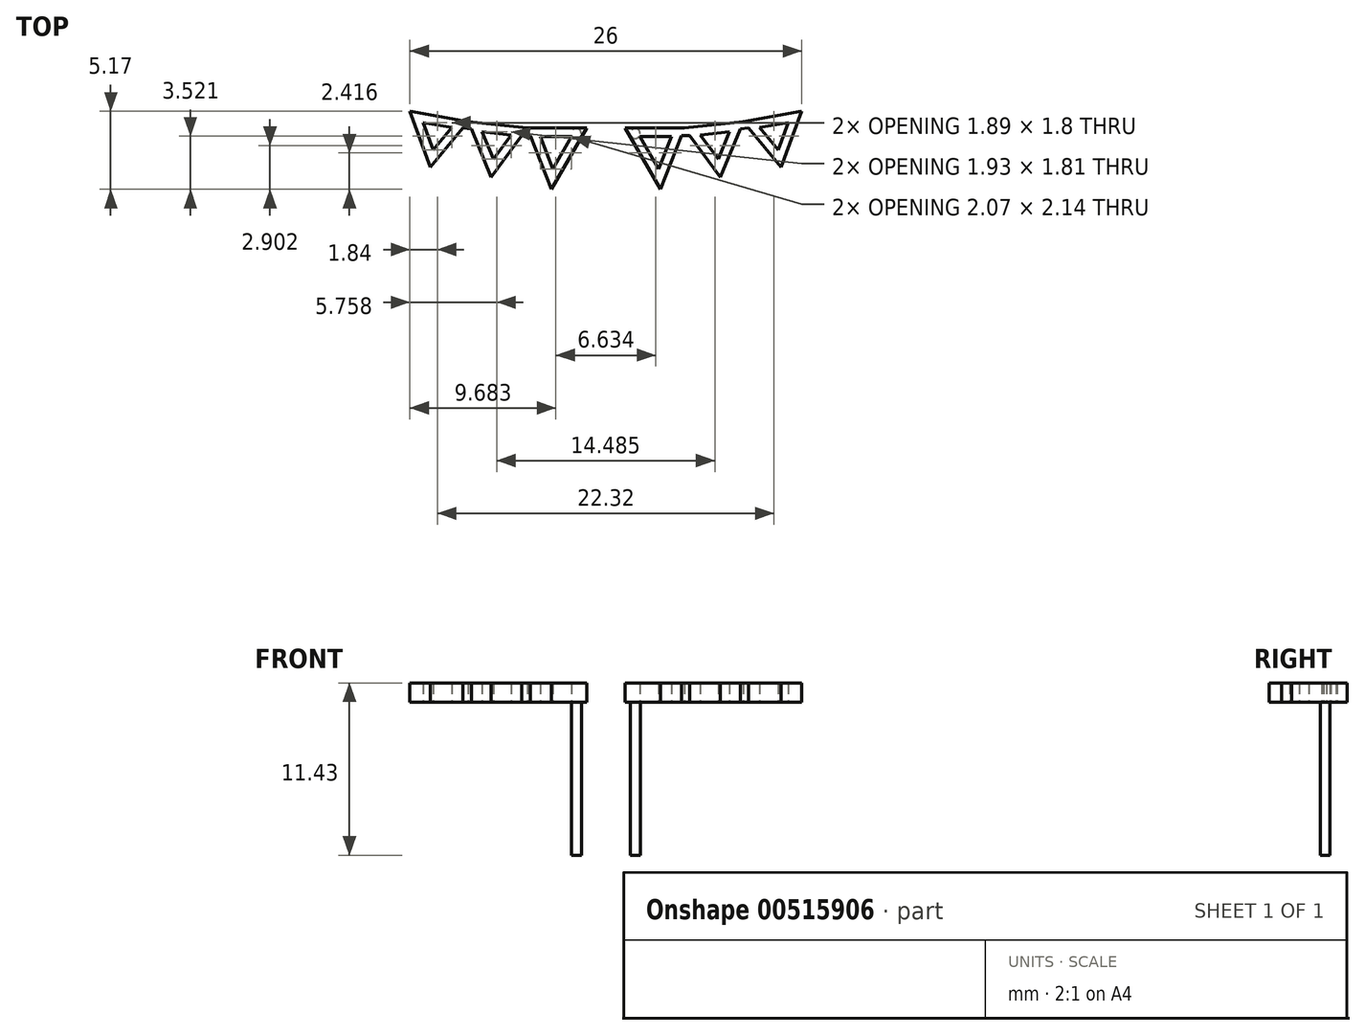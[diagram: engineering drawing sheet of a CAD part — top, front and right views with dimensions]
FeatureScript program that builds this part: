
annotation { "Feature Type Name" : "Feature", "Feature Type Description" : "" }
export const myFeature = defineFeature(function(context is Context, id is Id, definition is map)
    precondition{}
    {
        {
            var Q0;
            Q0=qCreatedBy(makeId("Top.planeOp"),FACE);
            var sketch = newSketch(context, id + "F0", { "sketchPlane" : qUnion([Q0])});
            skLineSegment(sketch, "E0", {"start": v(0, 0) * mm, "end": v(3.94, 0) * mm});
            skLineSegment(sketch, "E1", {"start": v(3.94, 0) * mm, "end": v(7.85, 0.43) * mm});
            skLineSegment(sketch, "E2", {"start": v(7.85, 0.43) * mm, "end": v(11.73, 1.1) * mm});
            skLineSegment(sketch, "E3", {"start": v(11.73, 1.1) * mm, "end": v(10.37, -2.6) * mm});
            skLineSegment(sketch, "E4", {"start": v(10.37, -2.6) * mm, "end": v(8.2, 0) * mm});
            skLineSegment(sketch, "E5", {"start": v(7.65, -0.06) * mm, "end": v(6.33, -3.26) * mm});
            skLineSegment(sketch, "E6", {"start": v(6.33, -3.26) * mm, "end": v(4.3, -0.5) * mm});
            skLineSegment(sketch, "E7", {"start": v(0, 0) * mm, "end": v(2.35, -4.07) * mm});
            skLineSegment(sketch, "E8", {"start": v(2.35, -4.07) * mm, "end": v(3.74, -0.5) * mm});
            skLineSegment(sketch, "E9.0", {"start": v(1.01, -0.58) * mm, "end": v(3.08, -0.58) * mm});
            skLineSegment(sketch, "E9.1", {"start": v(1.01, -0.58) * mm, "end": v(2.25, -2.72) * mm});
            skLineSegment(sketch, "E9.2", {"start": v(2.25, -2.72) * mm, "end": v(3.08, -0.58) * mm});
            skLineSegment(sketch, "E10.0", {"start": v(5, -0.47) * mm, "end": v(6.94, -0.26) * mm});
            skLineSegment(sketch, "E10.1", {"start": v(6.19, -2.08) * mm, "end": v(5, -0.47) * mm});
            skLineSegment(sketch, "E10.2", {"start": v(6.94, -0.26) * mm, "end": v(6.19, -2.08) * mm});
            skLineSegment(sketch, "E11.0", {"start": v(8.95, 0.02) * mm, "end": v(10.83, 0.35) * mm});
            skLineSegment(sketch, "E11.1", {"start": v(10.17, -1.45) * mm, "end": v(8.95, 0.02) * mm});
            skLineSegment(sketch, "E11.2", {"start": v(10.83, 0.35) * mm, "end": v(10.17, -1.45) * mm});
            skLineSegment(sketch, "E12", {"start": v(3.74, -0.5) * mm, "end": v(4.3, -0.5) * mm});
            skLineSegment(sketch, "E13", {"start": v(7.65, -0.06) * mm, "end": v(8.2, 0) * mm});
            skSolve(sketch);
        }
        {
            var Q0;
            Q0=makeQuery(id+"F0.imprint","IMPRINT",FACE,{"disambiguationData":[TD([[makeQuery(id+"F0.imprint","IMPRINT",EDGE,{"derivedFrom":sQuery(id+"F0.wireOp",EDGE,"E0")}),-1.0]])]});
            var Q1;
            Q1=makeQuery(id+"F0.imprint","IMPRINT",FACE,{"disambiguationData":[TD([[makeQuery(id+"F0.imprint","IMPRINT",EDGE,{"derivedFrom":sQuery(id+"F0.wireOp",EDGE,"E1")}),-1.0]])]});
            var Q2;
            Q2=makeQuery(id+"F0.imprint","IMPRINT",FACE,{"disambiguationData":[TD([[makeQuery(id+"F0.imprint","IMPRINT",EDGE,{"derivedFrom":sQuery(id+"F0.wireOp",EDGE,"E2")}),-1.0]])]});
            extrude(context, id + "F1", {"entities" : qUnion([Q0, Q1, Q2]), "depth" : 1.27 * mm, "offsetDistance" : 25.4 * mm});
        }
        {
            var Q0;
            Q0=makeQuery(id+"F1.opExtrude","CAP_FACE",FACE,{"disambiguationData":[OSD([sQuery(id+"F0.wireOp",EDGE,"E0"),sQuery(id+"F0.wireOp",EDGE,"E1"),sQuery(id+"F0.wireOp",EDGE,"E2"),sQuery(id+"F0.wireOp",EDGE,"E3"),sQuery(id+"F0.wireOp",EDGE,"E4"),sQuery(id+"F0.wireOp",EDGE,"E5"),sQuery(id+"F0.wireOp",EDGE,"E6"),sQuery(id+"F0.wireOp",EDGE,"E7"),sQuery(id+"F0.wireOp",EDGE,"E8"),sQuery(id+"F0.wireOp",EDGE,"E9.0"),sQuery(id+"F0.wireOp",EDGE,"E9.1"),sQuery(id+"F0.wireOp",EDGE,"E9.2"),sQuery(id+"F0.wireOp",EDGE,"E10.0"),sQuery(id+"F0.wireOp",EDGE,"E10.1"),sQuery(id+"F0.wireOp",EDGE,"E10.2"),sQuery(id+"F0.wireOp",EDGE,"E11.0"),sQuery(id+"F0.wireOp",EDGE,"E11.1"),sQuery(id+"F0.wireOp",EDGE,"E11.2"),sQuery(id+"F0.wireOp",EDGE,"E12"),sQuery(id+"F0.wireOp",EDGE,"E13")])],"isStart":true});
            var sketch = newSketch(context, id + "F2", { "sketchPlane" : qUnion([Q0])});
            skCircle(sketch, "E14", {"center": v(0.68, 0.37) * mm, "radius": 0.33 * mm});
            skSolve(sketch);
        }
        {
            var Q0;
            Q0 = qSketchRegion(id + "F2", true);
            extrude(context, id + "F3", {"entities" : qUnion([Q0]), "operationType" : NewBodyOperationType.ADD, "depth" : 10.16 * mm, "offsetDistance" : 25.4 * mm});
        }
        {
            var Q0;
            Q0=qCreatedBy(makeId("Right.planeOp"),FACE);
            cPlane(context, id + "F4", {"entities" : qUnion([Q0]), "cplaneType" : CPlaneType.OFFSET, "offset" : 1.27 * mm, "oppositeDirection" : true, "width" : 152.4 * mm, "height" : 152.4 * mm});
        }
        {
            var Q0;
            Q0=makeQuery(id+"F1.opExtrude","SWEPT_BODY",BODY,{"disambiguationData":[OSD([sQuery(id+"F0.wireOp",EDGE,"E0"),sQuery(id+"F0.wireOp",EDGE,"E1"),sQuery(id+"F0.wireOp",EDGE,"E2"),sQuery(id+"F0.wireOp",EDGE,"E3"),sQuery(id+"F0.wireOp",EDGE,"E4"),sQuery(id+"F0.wireOp",EDGE,"E5"),sQuery(id+"F0.wireOp",EDGE,"E6"),sQuery(id+"F0.wireOp",EDGE,"E7"),sQuery(id+"F0.wireOp",EDGE,"E8"),sQuery(id+"F0.wireOp",EDGE,"E9.0"),sQuery(id+"F0.wireOp",EDGE,"E9.1"),sQuery(id+"F0.wireOp",EDGE,"E9.2"),sQuery(id+"F0.wireOp",EDGE,"E10.0"),sQuery(id+"F0.wireOp",EDGE,"E10.1"),sQuery(id+"F0.wireOp",EDGE,"E10.2"),sQuery(id+"F0.wireOp",EDGE,"E11.0"),sQuery(id+"F0.wireOp",EDGE,"E11.1"),sQuery(id+"F0.wireOp",EDGE,"E11.2"),sQuery(id+"F0.wireOp",EDGE,"E12"),sQuery(id+"F0.wireOp",EDGE,"E13")])]});
            var Q1;
            Q1=qCreatedBy(id+"F4.planeOp",FACE);
            mirror(context, id + "F5", {"entities" : qUnion([Q0]), "mirrorPlane" : qUnion([Q1])});
        }
    });
